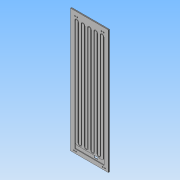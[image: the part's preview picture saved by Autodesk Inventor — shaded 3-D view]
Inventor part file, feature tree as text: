
AUTODESK INVENTOR PART (.ipt)
format: ipt  version: 2013 (Build 170138000, 138)  size: 277,504 bytes
history: native  units: in
note: dims shown in document units (in); Inventor stores cm internally (conversion verified against a paired STEP export)
features: other x12, extrude x3, hole x1
ambient origin geometry x8: Origin, YZ Plane, XZ Plane, XY Plane, X Axis, Y Axis, Z Axis, Center Point
bodies: Solid1 (feature_tree)
feature tree (16):
  other  "Blocks"
  extrude  "Stck Extrusion"  Depth=23.8125in
  extrude  "LED Extrusion3"  Depth=78.0in
  other  "Side profile reference"
  hole  "Hole1"  [1 undecoded]
  extrude  "Extrusion5"  Depth=66.0in
  other  "Stock"
  other  "LEDPocket"
  other  "TwoLineColumn"
  other  "TwoLineColumnEnd"
  other  "15mm Neon profile"
  other  "U Bolt hole and bore"
  other  "U-Bolt holes"
  other  "Through panel"
  other  "15mm Neon profile:1"
  other  "15mm Neon profile:2"
note: 1 required parameter value undecoded (feature->parameter linkage not recoverable at this tier; creation-order binding heuristic only, values carry confidence <= 0.55)
